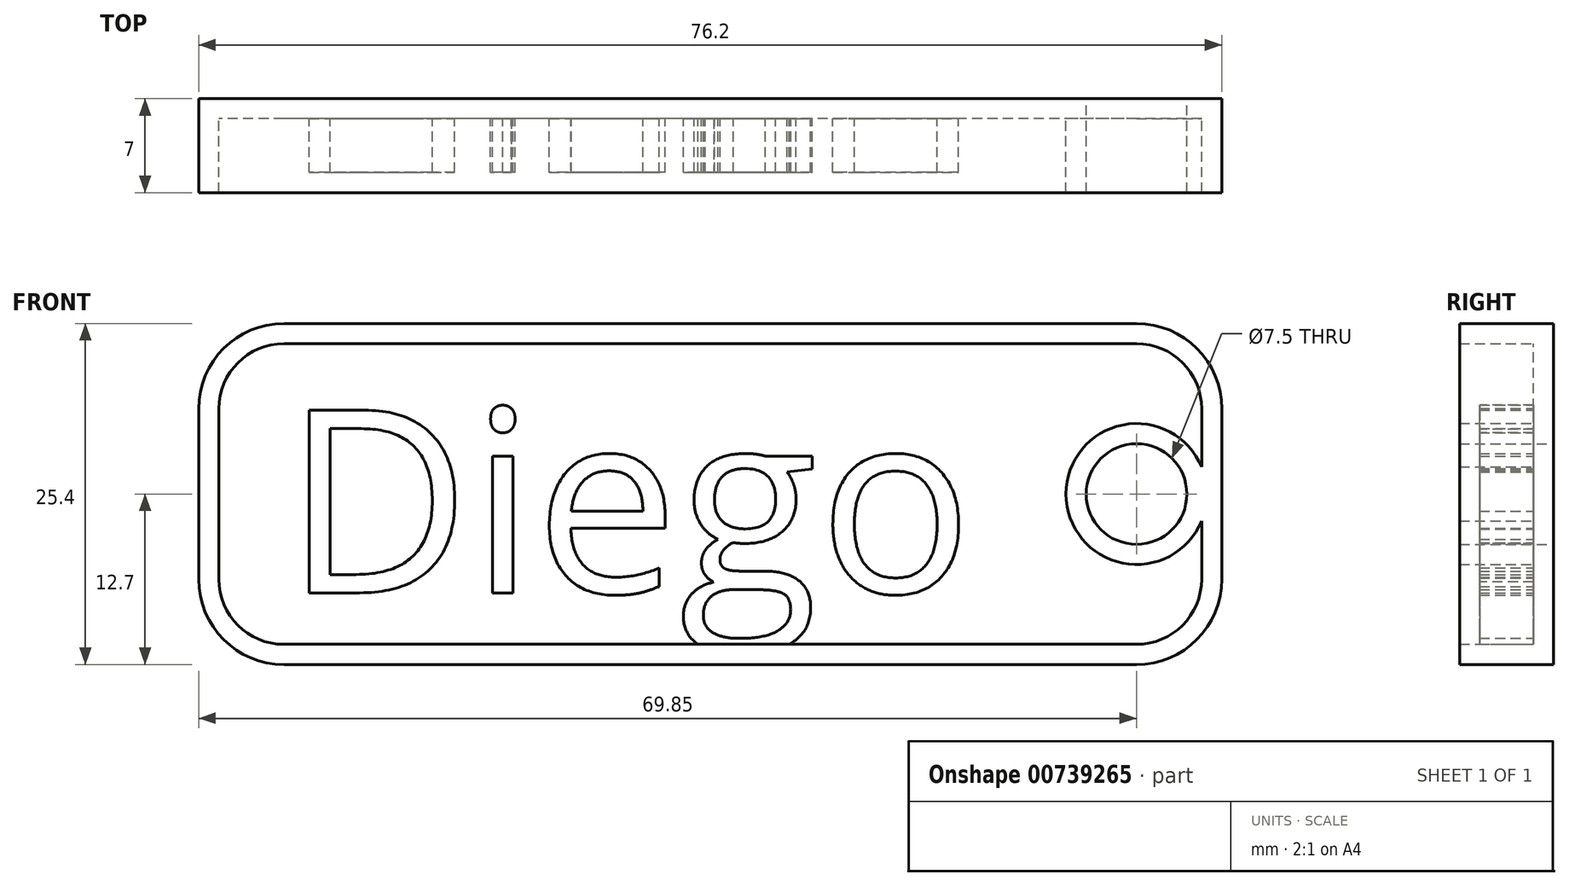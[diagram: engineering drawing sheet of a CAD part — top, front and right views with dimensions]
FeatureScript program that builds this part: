
annotation { "Feature Type Name" : "Feature", "Feature Type Description" : "" }
export const myFeature = defineFeature(function(context is Context, id is Id, definition is map)
    precondition{}
    {
        {
            var Q0;
            Q0=qCreatedBy(makeId("Front.planeOp"),FACE);
            var sketch = newSketch(context, id + "F0", { "sketchPlane" : qUnion([Q0])});
            skLineSegment(sketch, "E0.bottom", {"start": v(31.75, 12.7) * mm, "end": v(-31.75, 12.7) * mm});
            skLineSegment(sketch, "E0.top", {"start": v(31.75, -12.7) * mm, "end": v(-31.75, -12.7) * mm});
            skLineSegment(sketch, "E0.left", {"start": v(38.1, 6.35) * mm, "end": v(38.1, -6.35) * mm});
            skLineSegment(sketch, "E0.right", {"start": v(-38.1, 6.35) * mm, "end": v(-38.1, -6.35) * mm});
            skPoint(sketch, "E0.middle", {"position": v(0, 0) * mm});
            skPoint(sketch, "E1.visualSharp", {"position": v(38.1, 12.7) * mm});
            skArc(sketch, "E1.filletArc", {"start": v(38.1, 6.35) * mm, "mid": v(36.24, 10.84) * mm, "end": v(31.75, 12.7) * mm});
            skPoint(sketch, "E2.visualSharp", {"position": v(38.1, -12.7) * mm});
            skArc(sketch, "E2.filletArc", {"start": v(31.75, -12.7) * mm, "mid": v(36.24, -10.84) * mm, "end": v(38.1, -6.35) * mm});
            skPoint(sketch, "E3.visualSharp", {"position": v(-38.1, 12.7) * mm});
            skArc(sketch, "E3.filletArc", {"start": v(-31.75, 12.7) * mm, "mid": v(-36.24, 10.84) * mm, "end": v(-38.1, 6.35) * mm});
            skPoint(sketch, "E4.visualSharp", {"position": v(-38.1, -12.7) * mm});
            skArc(sketch, "E4.filletArc", {"start": v(-38.1, -6.35) * mm, "mid": v(-36.24, -10.84) * mm, "end": v(-31.75, -12.7) * mm});
            skCircle(sketch, "E5", {"center": v(31.75, 0) * mm, "radius": 3.75 * mm});
            skSolve(sketch);
        }
        {
            var Q0;
            Q0 = qSketchRegion(id + "F0", true);
            extrude(context, id + "F1", {"entities" : qUnion([Q0]), "depth" : 7 * mm, "offsetDistance" : 25 * mm});
        }
        {
            var Q0;
            Q0=makeQuery(id+"F1.opExtrude","CAP_FACE",FACE,{"disambiguationData":[OSD([sQuery(id+"F0.wireOp",EDGE,"E0.bottom"),sQuery(id+"F0.wireOp",EDGE,"E0.top"),sQuery(id+"F0.wireOp",EDGE,"E0.left"),sQuery(id+"F0.wireOp",EDGE,"E0.right"),sQuery(id+"F0.wireOp",EDGE,"E1.filletArc"),sQuery(id+"F0.wireOp",EDGE,"E2.filletArc"),sQuery(id+"F0.wireOp",EDGE,"E3.filletArc"),sQuery(id+"F0.wireOp",EDGE,"E4.filletArc")])],"isStart":false});
            var Q1;
            Q1=makeQuery(id+"F1.opExtrude","SWEPT_BODY",BODY,{"disambiguationData":[OSD([sQuery(id+"F0.wireOp",EDGE,"E0.bottom"),sQuery(id+"F0.wireOp",EDGE,"E0.top"),sQuery(id+"F0.wireOp",EDGE,"E0.left"),sQuery(id+"F0.wireOp",EDGE,"E0.right"),sQuery(id+"F0.wireOp",EDGE,"E1.filletArc"),sQuery(id+"F0.wireOp",EDGE,"E2.filletArc"),sQuery(id+"F0.wireOp",EDGE,"E3.filletArc"),sQuery(id+"F0.wireOp",EDGE,"E4.filletArc")])]});
            shell(context, id + "F2", {"entities" : qUnion([Q0]), "parts" : qUnion([Q1]), "thickness" : 1.5 * mm});
        }
        {
            var Q0;
            Q0=makeQuery(id+"F2.opShell","OFFSET_FACE",FACE,{"disambiguationData":[OSD([sQuery(id+"F0.wireOp",EDGE,"E0.bottom"),sQuery(id+"F0.wireOp",EDGE,"E0.top"),sQuery(id+"F0.wireOp",EDGE,"E0.left"),sQuery(id+"F0.wireOp",EDGE,"E0.right"),sQuery(id+"F0.wireOp",EDGE,"E1.filletArc"),sQuery(id+"F0.wireOp",EDGE,"E2.filletArc"),sQuery(id+"F0.wireOp",EDGE,"E3.filletArc"),sQuery(id+"F0.wireOp",EDGE,"E4.filletArc"),sQuery(id+"F0.wireOp",EDGE,"E5")])]});
            var sketch = newSketch(context, id + "F3", { "sketchPlane" : qUnion([Q0])});
            skText(sketch, "E6", { "text": "Diego", "fontName": "OpenSans-Regular.ttf"});
            const initialGuessF3  = {"E6": [-0.03175, -0.00736, 1, 0, 0.01371]};
            skSetInitialGuess(sketch, initialGuessF3);
            skSolve(sketch);
        }
        {
            var Q0;
            Q0 = qSketchRegion(id + "F3", true);
            extrude(context, id + "F4", {"entities" : qUnion([Q0]), "operationType" : NewBodyOperationType.ADD, "depth" : 4 * mm, "offsetDistance" : 25 * mm});
        }
    });
